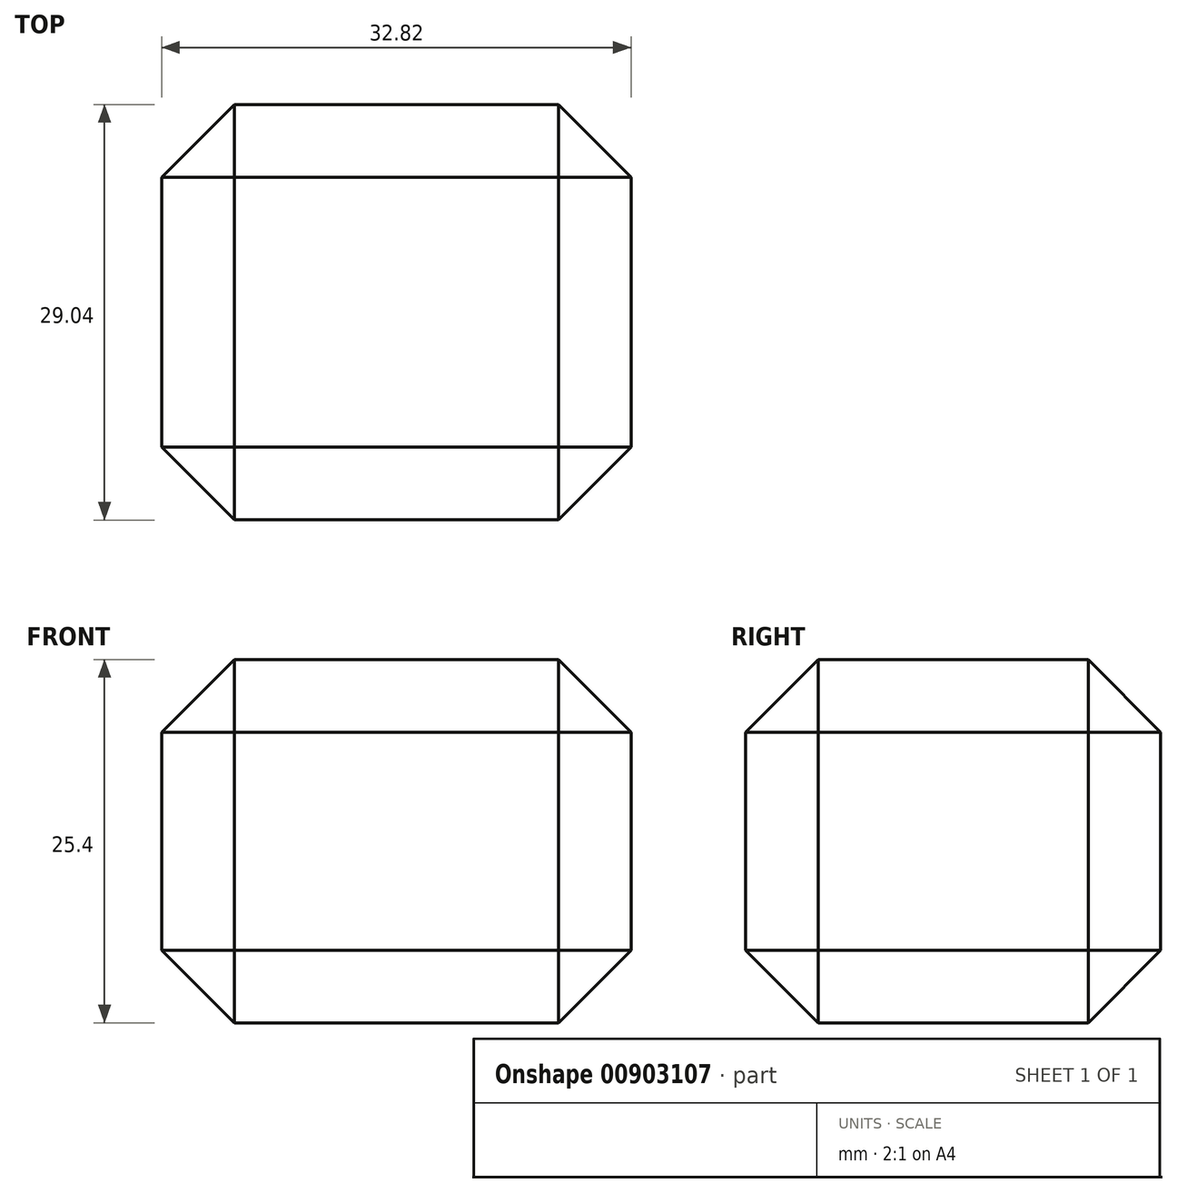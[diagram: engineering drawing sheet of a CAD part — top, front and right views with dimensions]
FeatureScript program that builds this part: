
annotation { "Feature Type Name" : "Feature", "Feature Type Description" : "" }
export const myFeature = defineFeature(function(context is Context, id is Id, definition is map)
    precondition{}
    {
        {
            var Q0;
            Q0=qCreatedBy(makeId("Top.planeOp"),FACE);
            var sketch = newSketch(context, id + "F0", { "sketchPlane" : qUnion([Q0])});
            skLineSegment(sketch, "E0.bottom", {"start": v(40.37, 40.56) * mm, "end": v(7.55, 40.56) * mm});
            skLineSegment(sketch, "E0.top", {"start": v(40.37, 11.52) * mm, "end": v(7.55, 11.52) * mm});
            skLineSegment(sketch, "E0.left", {"start": v(40.37, 40.56) * mm, "end": v(40.37, 11.52) * mm});
            skLineSegment(sketch, "E0.right", {"start": v(7.55, 40.56) * mm, "end": v(7.55, 11.52) * mm});
            skSolve(sketch);
        }
        {
            var Q0;
            Q0=makeQuery(id+"F0.imprint","IMPRINT",FACE,{"disambiguationData":[TD([[makeQuery(id+"F0.imprint","IMPRINT",EDGE,{"derivedFrom":sQuery(id+"F0.wireOp",EDGE,"E0.bottom")}),1.0]])]});
            extrude(context, id + "F1", {"entities" : qUnion([Q0]), "depth" : 25.4 * mm, "offsetDistance" : 25.4 * mm});
        }
        {
            var Q0;
            Q0=makeQuery(id+"F1.opExtrude","CAP_EDGE",EDGE,{"disambiguationData":[OSD([sQuery(id+"F0.wireOp",EDGE,"E0.bottom")])],"isStart":false});
            var Q1;
            Q1=makeQuery(id+"F1.opExtrude","CAP_EDGE",EDGE,{"disambiguationData":[OSD([sQuery(id+"F0.wireOp",EDGE,"E0.right")])],"isStart":false});
            var Q2;
            Q2=makeQuery(id+"F1.opExtrude","SWEPT_EDGE",EDGE,{"disambiguationData":[OSD([sQuery(id+"F0.wireOp",EDGE,"E0.bottom"),sQuery(id+"F0.wireOp",EDGE,"E0.right")])]});
            var Q3;
            Q3=makeQuery(id+"F1.opExtrude","SWEPT_EDGE",EDGE,{"disambiguationData":[OSD([sQuery(id+"F0.wireOp",EDGE,"E0.bottom"),sQuery(id+"F0.wireOp",EDGE,"E0.left")])]});
            var Q4;
            Q4=makeQuery(id+"F1.opExtrude","CAP_EDGE",EDGE,{"disambiguationData":[OSD([sQuery(id+"F0.wireOp",EDGE,"E0.left")])],"isStart":false});
            var Q5;
            Q5=makeQuery(id+"F1.opExtrude","SWEPT_EDGE",EDGE,{"disambiguationData":[OSD([sQuery(id+"F0.wireOp",EDGE,"E0.top"),sQuery(id+"F0.wireOp",EDGE,"E0.left")])]});
            var Q6;
            Q6=makeQuery(id+"F1.opExtrude","CAP_EDGE",EDGE,{"disambiguationData":[OSD([sQuery(id+"F0.wireOp",EDGE,"E0.top")])],"isStart":true});
            var Q7;
            Q7=makeQuery(id+"F1.opExtrude","CAP_EDGE",EDGE,{"disambiguationData":[OSD([sQuery(id+"F0.wireOp",EDGE,"E0.left")])],"isStart":true});
            var Q8;
            Q8=makeQuery(id+"F1.opExtrude","SWEPT_EDGE",EDGE,{"disambiguationData":[OSD([sQuery(id+"F0.wireOp",EDGE,"E0.top"),sQuery(id+"F0.wireOp",EDGE,"E0.right")])]});
            var Q9;
            Q9=makeQuery(id+"F1.opExtrude","CAP_EDGE",EDGE,{"disambiguationData":[OSD([sQuery(id+"F0.wireOp",EDGE,"E0.right")])],"isStart":true});
            var Q10;
            Q10=makeQuery(id+"F1.opExtrude","CAP_EDGE",EDGE,{"disambiguationData":[OSD([sQuery(id+"F0.wireOp",EDGE,"E0.bottom")])],"isStart":true});
            var Q11;
            Q11=makeQuery(id+"F1.opExtrude","CAP_EDGE",EDGE,{"disambiguationData":[OSD([sQuery(id+"F0.wireOp",EDGE,"E0.top")])],"isStart":false});
            chamfer(context, id + "F2", {"entities" : qUnion([Q0, Q1, Q2, Q3, Q4, Q5, Q6, Q7, Q8, Q9, Q10, Q11]), "width" : 5.08 * mm, "tangentPropagation" : true});
        }
    });
